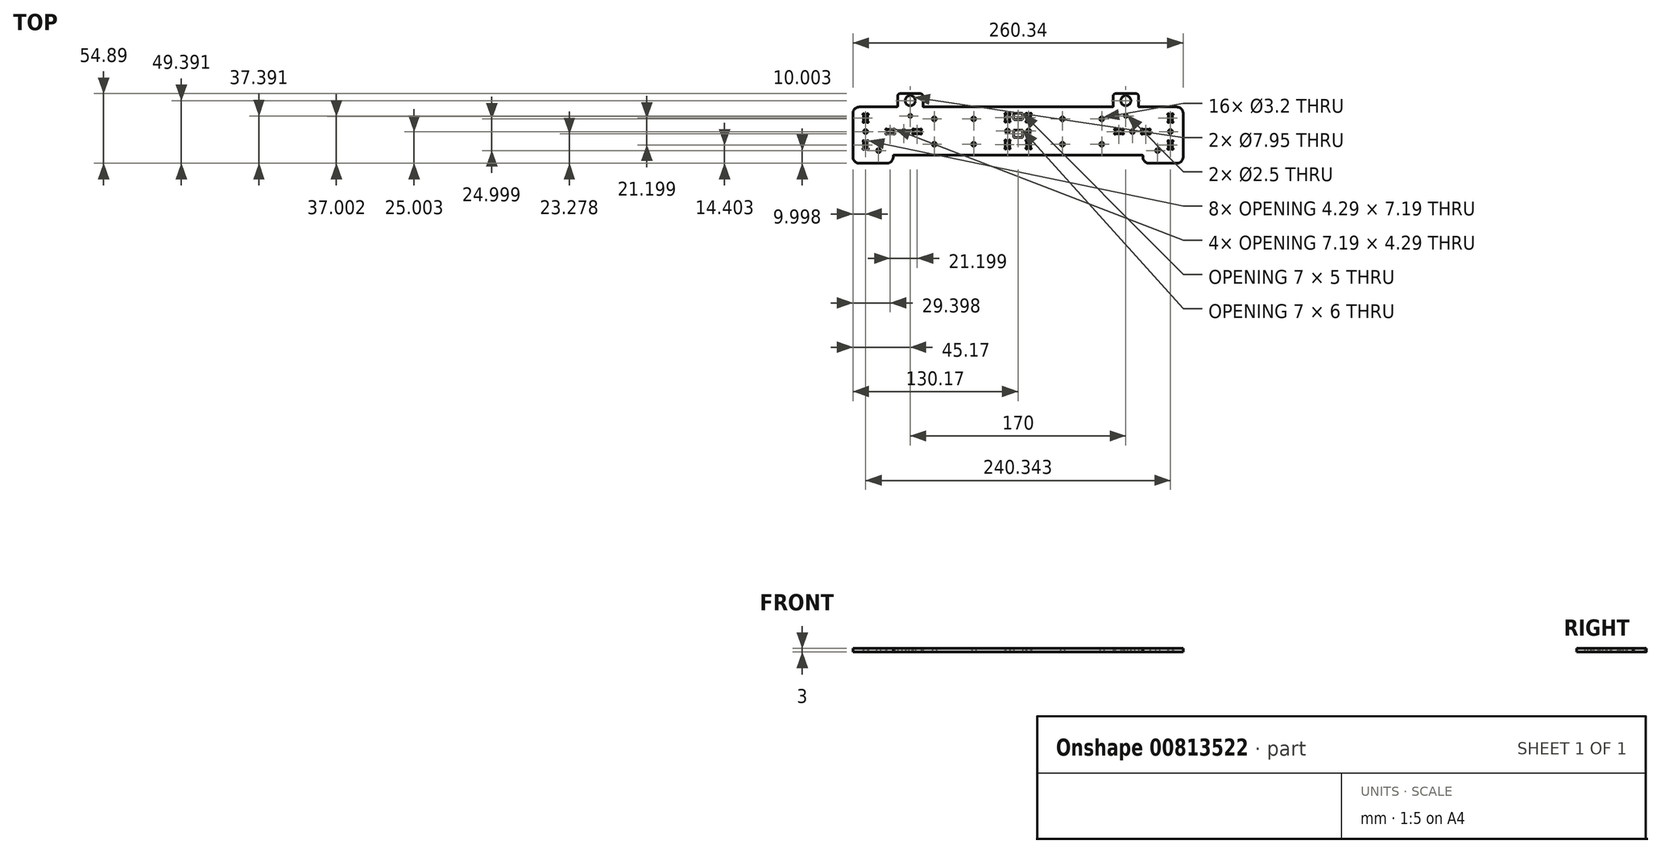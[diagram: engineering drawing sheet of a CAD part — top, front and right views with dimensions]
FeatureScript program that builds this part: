
annotation { "Feature Type Name" : "Feature", "Feature Type Description" : "" }
export const myFeature = defineFeature(function(context is Context, id is Id, definition is map)
    precondition{}
    {
        {
            var Q0;
            Q0=qCreatedBy(makeId("Top.planeOp"),FACE);
            var sketch = newSketch(context, id + "F0", { "sketchPlane" : qUnion([Q0])});
            skArc(sketch, "E0", {"start": v(-130.17, -20.39) * mm, "mid": v(-128.7, -23.92) * mm, "end": v(-125.17, -25.39) * mm});
            skLineSegment(sketch, "E1", {"start": v(-130.17, -20.39) * mm, "end": v(-130.17, 14) * mm});
            skArc(sketch, "E2", {"start": v(-125.17, 19) * mm, "mid": v(-128.7, 17.54) * mm, "end": v(-130.17, 14) * mm});
            skLineSegment(sketch, "E3", {"start": v(-125.17, 19) * mm, "end": v(-95.5, 19) * mm});
            skArc(sketch, "E4", {"start": v(-95.5, 19) * mm, "mid": v(-95.15, 19.15) * mm, "end": v(-95, 19.5) * mm});
            skArc(sketch, "E5", {"start": v(-75, 19.5) * mm, "mid": v(-74.85, 19.15) * mm, "end": v(-74.5, 19) * mm});
            skLineSegment(sketch, "E6", {"start": v(-74.5, 19) * mm, "end": v(74.5, 19) * mm});
            skArc(sketch, "E7", {"start": v(74.5, 19) * mm, "mid": v(74.85, 19.15) * mm, "end": v(75, 19.5) * mm});
            skArc(sketch, "E8", {"start": v(95, 19.5) * mm, "mid": v(95.15, 19.15) * mm, "end": v(95.5, 19) * mm});
            skLineSegment(sketch, "E9", {"start": v(95.5, 19) * mm, "end": v(125.17, 19) * mm});
            skArc(sketch, "E10", {"start": v(130.17, 14) * mm, "mid": v(128.7, 17.54) * mm, "end": v(125.17, 19) * mm});
            skLineSegment(sketch, "E11", {"start": v(130.17, 14) * mm, "end": v(130.17, -20.39) * mm});
            skArc(sketch, "E12", {"start": v(125.17, -25.39) * mm, "mid": v(128.7, -23.92) * mm, "end": v(130.17, -20.39) * mm});
            skArc(sketch, "E13", {"start": v(118.95, -7.64) * mm, "mid": v(119.14, -7.82) * mm, "end": v(119.39, -7.89) * mm});
            skArc(sketch, "E14", {"start": v(118.95, -7.64) * mm, "mid": v(118.17, -7.53) * mm, "end": v(118.27, -8.32) * mm});
            skArc(sketch, "E15", {"start": v(118.52, -8.75) * mm, "mid": v(118.45, -8.5) * mm, "end": v(118.27, -8.32) * mm});
            skLineSegment(sketch, "E16", {"start": v(118.52, -8.75) * mm, "end": v(118.52, -13.22) * mm});
            skArc(sketch, "E17", {"start": v(118.27, -13.65) * mm, "mid": v(118.45, -13.47) * mm, "end": v(118.52, -13.22) * mm});
            skArc(sketch, "E18", {"start": v(118.27, -13.65) * mm, "mid": v(118.17, -14.44) * mm, "end": v(118.95, -14.34) * mm});
            skArc(sketch, "E19", {"start": v(119.39, -14.09) * mm, "mid": v(119.14, -14.15) * mm, "end": v(118.95, -14.34) * mm});
            skLineSegment(sketch, "E20", {"start": v(119.39, -14.09) * mm, "end": v(120.96, -14.09) * mm});
            skArc(sketch, "E21", {"start": v(121.39, -14.34) * mm, "mid": v(121.2, -14.15) * mm, "end": v(120.96, -14.09) * mm});
            skArc(sketch, "E22", {"start": v(121.39, -14.34) * mm, "mid": v(122.17, -14.44) * mm, "end": v(122.07, -13.65) * mm});
            skArc(sketch, "E23", {"start": v(121.82, -13.22) * mm, "mid": v(121.89, -13.47) * mm, "end": v(122.07, -13.65) * mm});
            skLineSegment(sketch, "E24", {"start": v(121.82, -13.22) * mm, "end": v(121.82, -8.75) * mm});
            skArc(sketch, "E25", {"start": v(122.07, -8.32) * mm, "mid": v(121.89, -8.5) * mm, "end": v(121.82, -8.75) * mm});
            skArc(sketch, "E26", {"start": v(122.07, -8.32) * mm, "mid": v(122.17, -7.53) * mm, "end": v(121.39, -7.64) * mm});
            skArc(sketch, "E27", {"start": v(120.96, -7.89) * mm, "mid": v(121.2, -7.82) * mm, "end": v(121.39, -7.64) * mm});
            skLineSegment(sketch, "E28", {"start": v(120.96, -7.89) * mm, "end": v(119.39, -7.89) * mm});
            skArc(sketch, "E29", {"start": v(118.95, 13.56) * mm, "mid": v(119.14, 13.38) * mm, "end": v(119.39, 13.31) * mm});
            skArc(sketch, "E30", {"start": v(118.95, 13.56) * mm, "mid": v(118.17, 13.67) * mm, "end": v(118.27, 12.88) * mm});
            skArc(sketch, "E31", {"start": v(118.52, 12.45) * mm, "mid": v(118.45, 12.7) * mm, "end": v(118.27, 12.88) * mm});
            skLineSegment(sketch, "E32", {"start": v(118.52, 12.45) * mm, "end": v(118.52, 7.98) * mm});
            skArc(sketch, "E33", {"start": v(118.27, 7.55) * mm, "mid": v(118.45, 7.73) * mm, "end": v(118.52, 7.98) * mm});
            skArc(sketch, "E34", {"start": v(118.27, 7.55) * mm, "mid": v(118.17, 6.76) * mm, "end": v(118.95, 6.86) * mm});
            skArc(sketch, "E35", {"start": v(119.39, 7.11) * mm, "mid": v(119.14, 7.05) * mm, "end": v(118.95, 6.86) * mm});
            skLineSegment(sketch, "E36", {"start": v(119.39, 7.11) * mm, "end": v(120.96, 7.11) * mm});
            skArc(sketch, "E37", {"start": v(121.39, 6.86) * mm, "mid": v(121.2, 7.05) * mm, "end": v(120.96, 7.11) * mm});
            skArc(sketch, "E38", {"start": v(121.39, 6.86) * mm, "mid": v(122.17, 6.76) * mm, "end": v(122.07, 7.55) * mm});
            skArc(sketch, "E39", {"start": v(121.82, 7.98) * mm, "mid": v(121.89, 7.73) * mm, "end": v(122.07, 7.55) * mm});
            skLineSegment(sketch, "E40", {"start": v(121.82, 7.98) * mm, "end": v(121.82, 12.45) * mm});
            skArc(sketch, "E41", {"start": v(122.07, 12.88) * mm, "mid": v(121.89, 12.7) * mm, "end": v(121.82, 12.45) * mm});
            skArc(sketch, "E42", {"start": v(122.07, 12.88) * mm, "mid": v(122.17, 13.67) * mm, "end": v(121.39, 13.56) * mm});
            skArc(sketch, "E43", {"start": v(120.96, 13.31) * mm, "mid": v(121.2, 13.38) * mm, "end": v(121.39, 13.56) * mm});
            skLineSegment(sketch, "E44", {"start": v(120.96, 13.31) * mm, "end": v(119.39, 13.31) * mm});
            skArc(sketch, "E45", {"start": v(-119.39, -7.89) * mm, "mid": v(-119.14, -7.82) * mm, "end": v(-118.95, -7.64) * mm});
            skArc(sketch, "E46", {"start": v(-118.27, -8.32) * mm, "mid": v(-118.17, -7.53) * mm, "end": v(-118.95, -7.64) * mm});
            skArc(sketch, "E47", {"start": v(-118.27, -8.32) * mm, "mid": v(-118.45, -8.5) * mm, "end": v(-118.52, -8.75) * mm});
            skLineSegment(sketch, "E48", {"start": v(-118.52, -8.75) * mm, "end": v(-118.52, -13.22) * mm});
            skArc(sketch, "E49", {"start": v(-118.52, -13.22) * mm, "mid": v(-118.45, -13.47) * mm, "end": v(-118.27, -13.65) * mm});
            skArc(sketch, "E50", {"start": v(-118.95, -14.34) * mm, "mid": v(-118.17, -14.44) * mm, "end": v(-118.27, -13.65) * mm});
            skArc(sketch, "E51", {"start": v(-118.95, -14.34) * mm, "mid": v(-119.14, -14.15) * mm, "end": v(-119.39, -14.09) * mm});
            skLineSegment(sketch, "E52", {"start": v(-119.39, -14.09) * mm, "end": v(-120.96, -14.09) * mm});
            skArc(sketch, "E53", {"start": v(-120.96, -14.09) * mm, "mid": v(-121.2, -14.15) * mm, "end": v(-121.39, -14.34) * mm});
            skArc(sketch, "E54", {"start": v(-122.07, -13.65) * mm, "mid": v(-122.17, -14.44) * mm, "end": v(-121.39, -14.34) * mm});
            skArc(sketch, "E55", {"start": v(-122.07, -13.65) * mm, "mid": v(-121.89, -13.47) * mm, "end": v(-121.82, -13.22) * mm});
            skLineSegment(sketch, "E56", {"start": v(-121.82, -13.22) * mm, "end": v(-121.82, -8.75) * mm});
            skArc(sketch, "E57", {"start": v(-121.82, -8.75) * mm, "mid": v(-121.89, -8.5) * mm, "end": v(-122.07, -8.32) * mm});
            skArc(sketch, "E58", {"start": v(-121.39, -7.64) * mm, "mid": v(-122.17, -7.53) * mm, "end": v(-122.07, -8.32) * mm});
            skArc(sketch, "E59", {"start": v(-121.39, -7.64) * mm, "mid": v(-121.2, -7.82) * mm, "end": v(-120.96, -7.89) * mm});
            skLineSegment(sketch, "E60", {"start": v(-120.96, -7.89) * mm, "end": v(-119.39, -7.89) * mm});
            skArc(sketch, "E61", {"start": v(-119.39, 13.31) * mm, "mid": v(-119.14, 13.38) * mm, "end": v(-118.95, 13.56) * mm});
            skArc(sketch, "E62", {"start": v(-118.27, 12.88) * mm, "mid": v(-118.17, 13.67) * mm, "end": v(-118.95, 13.56) * mm});
            skArc(sketch, "E63", {"start": v(-118.27, 12.88) * mm, "mid": v(-118.45, 12.7) * mm, "end": v(-118.52, 12.45) * mm});
            skLineSegment(sketch, "E64", {"start": v(-118.52, 12.45) * mm, "end": v(-118.52, 7.98) * mm});
            skArc(sketch, "E65", {"start": v(-118.52, 7.98) * mm, "mid": v(-118.45, 7.73) * mm, "end": v(-118.27, 7.55) * mm});
            skArc(sketch, "E66", {"start": v(-118.95, 6.86) * mm, "mid": v(-118.17, 6.76) * mm, "end": v(-118.27, 7.55) * mm});
            skArc(sketch, "E67", {"start": v(-118.95, 6.86) * mm, "mid": v(-119.14, 7.05) * mm, "end": v(-119.39, 7.11) * mm});
            skLineSegment(sketch, "E68", {"start": v(-119.39, 7.11) * mm, "end": v(-120.96, 7.11) * mm});
            skArc(sketch, "E69", {"start": v(-120.96, 7.11) * mm, "mid": v(-121.2, 7.05) * mm, "end": v(-121.39, 6.86) * mm});
            skArc(sketch, "E70", {"start": v(-122.07, 7.55) * mm, "mid": v(-122.17, 6.76) * mm, "end": v(-121.39, 6.86) * mm});
            skArc(sketch, "E71", {"start": v(-122.07, 7.55) * mm, "mid": v(-121.89, 7.73) * mm, "end": v(-121.82, 7.98) * mm});
            skLineSegment(sketch, "E72", {"start": v(-121.82, 7.98) * mm, "end": v(-121.82, 12.45) * mm});
            skArc(sketch, "E73", {"start": v(-121.82, 12.45) * mm, "mid": v(-121.89, 12.7) * mm, "end": v(-122.07, 12.88) * mm});
            skArc(sketch, "E74", {"start": v(-121.39, 13.56) * mm, "mid": v(-122.17, 13.67) * mm, "end": v(-122.07, 12.88) * mm});
            skArc(sketch, "E75", {"start": v(-121.39, 13.56) * mm, "mid": v(-121.2, 13.38) * mm, "end": v(-120.96, 13.31) * mm});
            skLineSegment(sketch, "E76", {"start": v(-120.96, 13.31) * mm, "end": v(-119.39, 13.31) * mm});
            skCircle(sketch, "E77", {"center": v(120.17, -0.39) * mm, "radius": 1.6 * mm});
            skCircle(sketch, "E78", {"center": v(66, -10.39) * mm, "radius": 1.6 * mm});
            skCircle(sketch, "E79", {"center": v(66, 9.61) * mm, "radius": 1.6 * mm});
            skCircle(sketch, "E80", {"center": v(35, -10.39) * mm, "radius": 1.6 * mm});
            skCircle(sketch, "E81", {"center": v(35, 9.61) * mm, "radius": 1.6 * mm});
            skCircle(sketch, "E82", {"center": v(-35, -10.39) * mm, "radius": 1.6 * mm});
            skCircle(sketch, "E83", {"center": v(-35, 9.61) * mm, "radius": 1.6 * mm});
            skCircle(sketch, "E84", {"center": v(-66, -10.39) * mm, "radius": 1.6 * mm});
            skCircle(sketch, "E85", {"center": v(-66, 9.61) * mm, "radius": 1.6 * mm});
            skCircle(sketch, "E86", {"center": v(-120.17, -0.39) * mm, "radius": 1.6 * mm});
            skCircle(sketch, "E87", {"center": v(-85, 12) * mm, "radius": 1.25 * mm});
            skCircle(sketch, "E88", {"center": v(85, 12) * mm, "radius": 1.25 * mm});
            skArc(sketch, "E89", {"start": v(-97.42, 0.83) * mm, "mid": v(-97.6, 0.65) * mm, "end": v(-97.67, 0.4) * mm});
            skArc(sketch, "E90", {"start": v(-97.42, 0.83) * mm, "mid": v(-97.32, 1.62) * mm, "end": v(-98.1, 1.51) * mm});
            skArc(sketch, "E91", {"start": v(-98.54, 1.26) * mm, "mid": v(-98.29, 1.33) * mm, "end": v(-98.1, 1.51) * mm});
            skLineSegment(sketch, "E92", {"start": v(-98.54, 1.26) * mm, "end": v(-103, 1.26) * mm});
            skArc(sketch, "E93", {"start": v(-103.44, 1.51) * mm, "mid": v(-103.26, 1.33) * mm, "end": v(-103, 1.26) * mm});
            skArc(sketch, "E94", {"start": v(-103.44, 1.51) * mm, "mid": v(-104.23, 1.62) * mm, "end": v(-104.12, 0.83) * mm});
            skArc(sketch, "E95", {"start": v(-103.87, 0.4) * mm, "mid": v(-103.94, 0.65) * mm, "end": v(-104.12, 0.83) * mm});
            skLineSegment(sketch, "E96", {"start": v(-103.87, 0.4) * mm, "end": v(-103.87, -1.17) * mm});
            skArc(sketch, "E97", {"start": v(-104.12, -1.6) * mm, "mid": v(-103.94, -1.42) * mm, "end": v(-103.87, -1.17) * mm});
            skArc(sketch, "E98", {"start": v(-104.12, -1.6) * mm, "mid": v(-104.23, -2.4) * mm, "end": v(-103.44, -2.29) * mm});
            skArc(sketch, "E99", {"start": v(-103, -2.04) * mm, "mid": v(-103.26, -2.1) * mm, "end": v(-103.44, -2.29) * mm});
            skLineSegment(sketch, "E100", {"start": v(-103, -2.04) * mm, "end": v(-98.54, -2.04) * mm});
            skArc(sketch, "E101", {"start": v(-98.1, -2.29) * mm, "mid": v(-98.29, -2.1) * mm, "end": v(-98.54, -2.04) * mm});
            skArc(sketch, "E102", {"start": v(-98.1, -2.29) * mm, "mid": v(-97.32, -2.4) * mm, "end": v(-97.42, -1.6) * mm});
            skArc(sketch, "E103", {"start": v(-97.67, -1.17) * mm, "mid": v(-97.6, -1.42) * mm, "end": v(-97.42, -1.6) * mm});
            skLineSegment(sketch, "E104", {"start": v(-97.67, -1.17) * mm, "end": v(-97.67, 0.4) * mm});
            skArc(sketch, "E105", {"start": v(-76.22, 0.83) * mm, "mid": v(-76.4, 0.65) * mm, "end": v(-76.47, 0.4) * mm});
            skArc(sketch, "E106", {"start": v(-76.22, 0.83) * mm, "mid": v(-76.12, 1.62) * mm, "end": v(-76.9, 1.51) * mm});
            skArc(sketch, "E107", {"start": v(-77.34, 1.26) * mm, "mid": v(-77.09, 1.33) * mm, "end": v(-76.9, 1.51) * mm});
            skLineSegment(sketch, "E108", {"start": v(-77.34, 1.26) * mm, "end": v(-81.8, 1.26) * mm});
            skArc(sketch, "E109", {"start": v(-82.24, 1.51) * mm, "mid": v(-82.06, 1.33) * mm, "end": v(-81.8, 1.26) * mm});
            skArc(sketch, "E110", {"start": v(-82.24, 1.51) * mm, "mid": v(-83.03, 1.62) * mm, "end": v(-82.92, 0.83) * mm});
            skArc(sketch, "E111", {"start": v(-82.67, 0.4) * mm, "mid": v(-82.74, 0.65) * mm, "end": v(-82.92, 0.83) * mm});
            skLineSegment(sketch, "E112", {"start": v(-82.67, 0.4) * mm, "end": v(-82.67, -1.17) * mm});
            skArc(sketch, "E113", {"start": v(-82.92, -1.6) * mm, "mid": v(-82.74, -1.42) * mm, "end": v(-82.67, -1.17) * mm});
            skArc(sketch, "E114", {"start": v(-82.92, -1.6) * mm, "mid": v(-83.03, -2.4) * mm, "end": v(-82.24, -2.29) * mm});
            skArc(sketch, "E115", {"start": v(-81.8, -2.04) * mm, "mid": v(-82.06, -2.1) * mm, "end": v(-82.24, -2.29) * mm});
            skLineSegment(sketch, "E116", {"start": v(-81.8, -2.04) * mm, "end": v(-77.34, -2.04) * mm});
            skArc(sketch, "E117", {"start": v(-76.9, -2.29) * mm, "mid": v(-77.09, -2.1) * mm, "end": v(-77.34, -2.04) * mm});
            skArc(sketch, "E118", {"start": v(-76.9, -2.29) * mm, "mid": v(-76.12, -2.4) * mm, "end": v(-76.22, -1.6) * mm});
            skArc(sketch, "E119", {"start": v(-76.47, -1.17) * mm, "mid": v(-76.4, -1.42) * mm, "end": v(-76.22, -1.6) * mm});
            skLineSegment(sketch, "E120", {"start": v(-76.47, -1.17) * mm, "end": v(-76.47, 0.4) * mm});
            skCircle(sketch, "E121", {"center": v(-90.17, -0.39) * mm, "radius": 1.6 * mm});
            skArc(sketch, "E122", {"start": v(82.92, 0.83) * mm, "mid": v(82.74, 0.65) * mm, "end": v(82.67, 0.4) * mm});
            skArc(sketch, "E123", {"start": v(82.92, 0.83) * mm, "mid": v(83.03, 1.62) * mm, "end": v(82.24, 1.51) * mm});
            skArc(sketch, "E124", {"start": v(81.8, 1.26) * mm, "mid": v(82.06, 1.33) * mm, "end": v(82.24, 1.51) * mm});
            skLineSegment(sketch, "E125", {"start": v(81.8, 1.26) * mm, "end": v(77.34, 1.26) * mm});
            skArc(sketch, "E126", {"start": v(76.9, 1.51) * mm, "mid": v(77.09, 1.33) * mm, "end": v(77.34, 1.26) * mm});
            skArc(sketch, "E127", {"start": v(76.9, 1.51) * mm, "mid": v(76.12, 1.62) * mm, "end": v(76.22, 0.83) * mm});
            skArc(sketch, "E128", {"start": v(76.47, 0.4) * mm, "mid": v(76.4, 0.65) * mm, "end": v(76.22, 0.83) * mm});
            skLineSegment(sketch, "E129", {"start": v(76.47, 0.4) * mm, "end": v(76.47, -1.17) * mm});
            skArc(sketch, "E130", {"start": v(76.22, -1.6) * mm, "mid": v(76.4, -1.42) * mm, "end": v(76.47, -1.17) * mm});
            skArc(sketch, "E131", {"start": v(76.22, -1.6) * mm, "mid": v(76.12, -2.4) * mm, "end": v(76.9, -2.29) * mm});
            skArc(sketch, "E132", {"start": v(77.34, -2.04) * mm, "mid": v(77.09, -2.1) * mm, "end": v(76.9, -2.29) * mm});
            skLineSegment(sketch, "E133", {"start": v(77.34, -2.04) * mm, "end": v(81.8, -2.04) * mm});
            skArc(sketch, "E134", {"start": v(82.24, -2.29) * mm, "mid": v(82.06, -2.1) * mm, "end": v(81.8, -2.04) * mm});
            skArc(sketch, "E135", {"start": v(82.24, -2.29) * mm, "mid": v(83.03, -2.4) * mm, "end": v(82.92, -1.6) * mm});
            skArc(sketch, "E136", {"start": v(82.67, -1.17) * mm, "mid": v(82.74, -1.42) * mm, "end": v(82.92, -1.6) * mm});
            skLineSegment(sketch, "E137", {"start": v(82.67, -1.17) * mm, "end": v(82.67, 0.4) * mm});
            skArc(sketch, "E138", {"start": v(104.12, 0.83) * mm, "mid": v(103.94, 0.65) * mm, "end": v(103.87, 0.4) * mm});
            skArc(sketch, "E139", {"start": v(104.12, 0.83) * mm, "mid": v(104.23, 1.62) * mm, "end": v(103.44, 1.51) * mm});
            skArc(sketch, "E140", {"start": v(103, 1.26) * mm, "mid": v(103.26, 1.33) * mm, "end": v(103.44, 1.51) * mm});
            skLineSegment(sketch, "E141", {"start": v(103, 1.26) * mm, "end": v(98.54, 1.26) * mm});
            skArc(sketch, "E142", {"start": v(98.1, 1.51) * mm, "mid": v(98.29, 1.33) * mm, "end": v(98.54, 1.26) * mm});
            skArc(sketch, "E143", {"start": v(98.1, 1.51) * mm, "mid": v(97.32, 1.62) * mm, "end": v(97.42, 0.83) * mm});
            skArc(sketch, "E144", {"start": v(97.67, 0.4) * mm, "mid": v(97.6, 0.65) * mm, "end": v(97.42, 0.83) * mm});
            skLineSegment(sketch, "E145", {"start": v(97.67, 0.4) * mm, "end": v(97.67, -1.17) * mm});
            skArc(sketch, "E146", {"start": v(97.42, -1.6) * mm, "mid": v(97.6, -1.42) * mm, "end": v(97.67, -1.17) * mm});
            skArc(sketch, "E147", {"start": v(97.42, -1.6) * mm, "mid": v(97.32, -2.4) * mm, "end": v(98.1, -2.29) * mm});
            skArc(sketch, "E148", {"start": v(98.54, -2.04) * mm, "mid": v(98.29, -2.1) * mm, "end": v(98.1, -2.29) * mm});
            skLineSegment(sketch, "E149", {"start": v(98.54, -2.04) * mm, "end": v(103, -2.04) * mm});
            skArc(sketch, "E150", {"start": v(103.44, -2.29) * mm, "mid": v(103.26, -2.1) * mm, "end": v(103, -2.04) * mm});
            skArc(sketch, "E151", {"start": v(103.44, -2.29) * mm, "mid": v(104.23, -2.4) * mm, "end": v(104.12, -1.6) * mm});
            skArc(sketch, "E152", {"start": v(103.87, -1.17) * mm, "mid": v(103.94, -1.42) * mm, "end": v(104.12, -1.6) * mm});
            skLineSegment(sketch, "E153", {"start": v(103.87, -1.17) * mm, "end": v(103.87, 0.4) * mm});
            skCircle(sketch, "E154", {"center": v(90.17, -0.39) * mm, "radius": 1.6 * mm});
            skLineSegment(sketch, "E155", {"start": v(-103.44, -25.39) * mm, "end": v(-125.17, -25.39) * mm});
            skArc(sketch, "E156", {"start": v(-103.44, -25.39) * mm, "mid": v(-99.9, -23.92) * mm, "end": v(-98.44, -20.39) * mm});
            skLineSegment(sketch, "E157", {"start": v(125.17, -25.39) * mm, "end": v(103.44, -25.39) * mm});
            skArc(sketch, "E158", {"start": v(98.44, -20.39) * mm, "mid": v(99.9, -23.92) * mm, "end": v(103.44, -25.39) * mm});
            skLineSegment(sketch, "E159", {"start": v(-98.44, -20.39) * mm, "end": v(-98.44, -19.5) * mm});
            skArc(sketch, "E160", {"start": v(-97.94, -19) * mm, "mid": v(-98.3, -19.15) * mm, "end": v(-98.44, -19.5) * mm});
            skLineSegment(sketch, "E161", {"start": v(98.44, -20.39) * mm, "end": v(98.44, -19.5) * mm});
            skLineSegment(sketch, "E162", {"start": v(-97.94, -19) * mm, "end": v(97.94, -19) * mm});
            skArc(sketch, "E163", {"start": v(98.44, -19.5) * mm, "mid": v(98.3, -19.15) * mm, "end": v(97.94, -19) * mm});
            skCircle(sketch, "E164", {"center": v(-8.3, 0) * mm, "radius": 1.6 * mm});
            skArc(sketch, "E165", {"start": v(-9.52, -7.25) * mm, "mid": v(-9.33, -7.43) * mm, "end": v(-9.08, -7.5) * mm});
            skArc(sketch, "E166", {"start": v(-9.52, -7.25) * mm, "mid": v(-10.3, -7.15) * mm, "end": v(-10.2, -7.93) * mm});
            skArc(sketch, "E167", {"start": v(-9.95, -8.37) * mm, "mid": v(-10.02, -8.12) * mm, "end": v(-10.2, -7.93) * mm});
            skLineSegment(sketch, "E168", {"start": v(-9.95, -8.37) * mm, "end": v(-9.95, -12.83) * mm});
            skArc(sketch, "E169", {"start": v(-10.2, -13.27) * mm, "mid": v(-10.02, -13.08) * mm, "end": v(-9.95, -12.83) * mm});
            skArc(sketch, "E170", {"start": v(-10.2, -13.27) * mm, "mid": v(-10.3, -14.05) * mm, "end": v(-9.52, -13.95) * mm});
            skArc(sketch, "E171", {"start": v(-9.08, -13.7) * mm, "mid": v(-9.33, -13.77) * mm, "end": v(-9.52, -13.95) * mm});
            skLineSegment(sketch, "E172", {"start": v(-9.08, -13.7) * mm, "end": v(-7.52, -13.7) * mm});
            skArc(sketch, "E173", {"start": v(-7.08, -13.95) * mm, "mid": v(-7.27, -13.77) * mm, "end": v(-7.52, -13.7) * mm});
            skArc(sketch, "E174", {"start": v(-7.08, -13.95) * mm, "mid": v(-6.3, -14.05) * mm, "end": v(-6.4, -13.27) * mm});
            skArc(sketch, "E175", {"start": v(-6.65, -12.83) * mm, "mid": v(-6.58, -13.08) * mm, "end": v(-6.4, -13.27) * mm});
            skLineSegment(sketch, "E176", {"start": v(-6.65, -12.83) * mm, "end": v(-6.65, -8.37) * mm});
            skArc(sketch, "E177", {"start": v(-6.4, -7.93) * mm, "mid": v(-6.58, -8.12) * mm, "end": v(-6.65, -8.37) * mm});
            skArc(sketch, "E178", {"start": v(-6.4, -7.93) * mm, "mid": v(-6.3, -7.15) * mm, "end": v(-7.08, -7.25) * mm});
            skArc(sketch, "E179", {"start": v(-7.52, -7.5) * mm, "mid": v(-7.27, -7.43) * mm, "end": v(-7.08, -7.25) * mm});
            skLineSegment(sketch, "E180", {"start": v(-7.52, -7.5) * mm, "end": v(-9.08, -7.5) * mm});
            skArc(sketch, "E181", {"start": v(-9.52, 13.95) * mm, "mid": v(-9.33, 13.77) * mm, "end": v(-9.08, 13.7) * mm});
            skArc(sketch, "E182", {"start": v(-9.52, 13.95) * mm, "mid": v(-10.3, 14.05) * mm, "end": v(-10.2, 13.27) * mm});
            skArc(sketch, "E183", {"start": v(-9.95, 12.83) * mm, "mid": v(-10.02, 13.08) * mm, "end": v(-10.2, 13.27) * mm});
            skLineSegment(sketch, "E184", {"start": v(-9.95, 12.83) * mm, "end": v(-9.95, 8.37) * mm});
            skArc(sketch, "E185", {"start": v(-10.2, 7.93) * mm, "mid": v(-10.02, 8.12) * mm, "end": v(-9.95, 8.37) * mm});
            skArc(sketch, "E186", {"start": v(-10.2, 7.93) * mm, "mid": v(-10.3, 7.15) * mm, "end": v(-9.52, 7.25) * mm});
            skArc(sketch, "E187", {"start": v(-9.08, 7.5) * mm, "mid": v(-9.33, 7.43) * mm, "end": v(-9.52, 7.25) * mm});
            skLineSegment(sketch, "E188", {"start": v(-9.08, 7.5) * mm, "end": v(-7.52, 7.5) * mm});
            skArc(sketch, "E189", {"start": v(-7.08, 7.25) * mm, "mid": v(-7.27, 7.43) * mm, "end": v(-7.52, 7.5) * mm});
            skArc(sketch, "E190", {"start": v(-7.08, 7.25) * mm, "mid": v(-6.3, 7.15) * mm, "end": v(-6.4, 7.93) * mm});
            skArc(sketch, "E191", {"start": v(-6.65, 8.37) * mm, "mid": v(-6.58, 8.12) * mm, "end": v(-6.4, 7.93) * mm});
            skLineSegment(sketch, "E192", {"start": v(-6.65, 8.37) * mm, "end": v(-6.65, 12.83) * mm});
            skArc(sketch, "E193", {"start": v(-6.4, 13.27) * mm, "mid": v(-6.58, 13.08) * mm, "end": v(-6.65, 12.83) * mm});
            skArc(sketch, "E194", {"start": v(-6.4, 13.27) * mm, "mid": v(-6.3, 14.05) * mm, "end": v(-7.08, 13.95) * mm});
            skArc(sketch, "E195", {"start": v(-7.52, 13.7) * mm, "mid": v(-7.27, 13.77) * mm, "end": v(-7.08, 13.95) * mm});
            skLineSegment(sketch, "E196", {"start": v(-7.52, 13.7) * mm, "end": v(-9.08, 13.7) * mm});
            skCircle(sketch, "E197", {"center": v(8.3, 0) * mm, "radius": 1.6 * mm});
            skArc(sketch, "E198", {"start": v(7.08, -7.25) * mm, "mid": v(7.27, -7.43) * mm, "end": v(7.52, -7.5) * mm});
            skArc(sketch, "E199", {"start": v(7.08, -7.25) * mm, "mid": v(6.3, -7.15) * mm, "end": v(6.4, -7.93) * mm});
            skArc(sketch, "E200", {"start": v(6.65, -8.37) * mm, "mid": v(6.58, -8.12) * mm, "end": v(6.4, -7.93) * mm});
            skLineSegment(sketch, "E201", {"start": v(6.65, -8.37) * mm, "end": v(6.65, -12.83) * mm});
            skArc(sketch, "E202", {"start": v(6.4, -13.27) * mm, "mid": v(6.58, -13.08) * mm, "end": v(6.65, -12.83) * mm});
            skArc(sketch, "E203", {"start": v(6.4, -13.27) * mm, "mid": v(6.3, -14.05) * mm, "end": v(7.08, -13.95) * mm});
            skArc(sketch, "E204", {"start": v(7.52, -13.7) * mm, "mid": v(7.27, -13.77) * mm, "end": v(7.08, -13.95) * mm});
            skLineSegment(sketch, "E205", {"start": v(7.52, -13.7) * mm, "end": v(9.08, -13.7) * mm});
            skArc(sketch, "E206", {"start": v(9.52, -13.95) * mm, "mid": v(9.33, -13.77) * mm, "end": v(9.08, -13.7) * mm});
            skArc(sketch, "E207", {"start": v(9.52, -13.95) * mm, "mid": v(10.3, -14.05) * mm, "end": v(10.2, -13.27) * mm});
            skArc(sketch, "E208", {"start": v(9.95, -12.83) * mm, "mid": v(10.02, -13.08) * mm, "end": v(10.2, -13.27) * mm});
            skLineSegment(sketch, "E209", {"start": v(9.95, -12.83) * mm, "end": v(9.95, -8.37) * mm});
            skArc(sketch, "E210", {"start": v(10.2, -7.93) * mm, "mid": v(10.02, -8.12) * mm, "end": v(9.95, -8.37) * mm});
            skArc(sketch, "E211", {"start": v(10.2, -7.93) * mm, "mid": v(10.3, -7.15) * mm, "end": v(9.52, -7.25) * mm});
            skArc(sketch, "E212", {"start": v(9.08, -7.5) * mm, "mid": v(9.33, -7.43) * mm, "end": v(9.52, -7.25) * mm});
            skLineSegment(sketch, "E213", {"start": v(9.08, -7.5) * mm, "end": v(7.52, -7.5) * mm});
            skArc(sketch, "E214", {"start": v(7.08, 13.95) * mm, "mid": v(7.27, 13.77) * mm, "end": v(7.52, 13.7) * mm});
            skArc(sketch, "E215", {"start": v(7.08, 13.95) * mm, "mid": v(6.3, 14.05) * mm, "end": v(6.4, 13.27) * mm});
            skArc(sketch, "E216", {"start": v(6.65, 12.83) * mm, "mid": v(6.58, 13.08) * mm, "end": v(6.4, 13.27) * mm});
            skLineSegment(sketch, "E217", {"start": v(6.65, 12.83) * mm, "end": v(6.65, 8.37) * mm});
            skArc(sketch, "E218", {"start": v(6.4, 7.93) * mm, "mid": v(6.58, 8.12) * mm, "end": v(6.65, 8.37) * mm});
            skArc(sketch, "E219", {"start": v(6.4, 7.93) * mm, "mid": v(6.3, 7.15) * mm, "end": v(7.08, 7.25) * mm});
            skArc(sketch, "E220", {"start": v(7.52, 7.5) * mm, "mid": v(7.27, 7.43) * mm, "end": v(7.08, 7.25) * mm});
            skLineSegment(sketch, "E221", {"start": v(7.52, 7.5) * mm, "end": v(9.08, 7.5) * mm});
            skArc(sketch, "E222", {"start": v(9.52, 7.25) * mm, "mid": v(9.33, 7.43) * mm, "end": v(9.08, 7.5) * mm});
            skArc(sketch, "E223", {"start": v(9.52, 7.25) * mm, "mid": v(10.3, 7.15) * mm, "end": v(10.2, 7.93) * mm});
            skArc(sketch, "E224", {"start": v(9.95, 8.37) * mm, "mid": v(10.02, 8.12) * mm, "end": v(10.2, 7.93) * mm});
            skLineSegment(sketch, "E225", {"start": v(9.95, 8.37) * mm, "end": v(9.95, 12.83) * mm});
            skArc(sketch, "E226", {"start": v(10.2, 13.27) * mm, "mid": v(10.02, 13.08) * mm, "end": v(9.95, 12.83) * mm});
            skArc(sketch, "E227", {"start": v(10.2, 13.27) * mm, "mid": v(10.3, 14.05) * mm, "end": v(9.52, 13.95) * mm});
            skArc(sketch, "E228", {"start": v(9.08, 13.7) * mm, "mid": v(9.33, 13.77) * mm, "end": v(9.52, 13.95) * mm});
            skLineSegment(sketch, "E229", {"start": v(9.08, 13.7) * mm, "end": v(7.52, 13.7) * mm});
            skCircle(sketch, "E230", {"center": v(-85, 24) * mm, "radius": 3.97 * mm});
            skCircle(sketch, "E231", {"center": v(85, 24) * mm, "radius": 3.97 * mm});
            skLineSegment(sketch, "E232", {"start": v(-95, 19.5) * mm, "end": v(-95, 27.5) * mm});
            skLineSegment(sketch, "E233", {"start": v(-75, 27.5) * mm, "end": v(-75, 19.5) * mm});
            skArc(sketch, "E234", {"start": v(-93, 29.5) * mm, "mid": v(-94.41, 28.92) * mm, "end": v(-95, 27.5) * mm});
            skLineSegment(sketch, "E235", {"start": v(-93, 29.5) * mm, "end": v(-77, 29.5) * mm});
            skArc(sketch, "E236", {"start": v(-75, 27.5) * mm, "mid": v(-75.59, 28.92) * mm, "end": v(-77, 29.5) * mm});
            skLineSegment(sketch, "E237", {"start": v(75, 19.5) * mm, "end": v(75, 27.5) * mm});
            skLineSegment(sketch, "E238", {"start": v(95, 27.5) * mm, "end": v(95, 19.5) * mm});
            skArc(sketch, "E239", {"start": v(77, 29.5) * mm, "mid": v(75.59, 28.92) * mm, "end": v(75, 27.5) * mm});
            skLineSegment(sketch, "E240", {"start": v(77, 29.5) * mm, "end": v(93, 29.5) * mm});
            skArc(sketch, "E241", {"start": v(95, 27.5) * mm, "mid": v(94.41, 28.92) * mm, "end": v(93, 29.5) * mm});
            skArc(sketch, "E242", {"start": v(-3.5, 9.51) * mm, "mid": v(-3.38, 9.23) * mm, "end": v(-3.1, 9.11) * mm});
            skLineSegment(sketch, "E243", {"start": v(3.1, 9.11) * mm, "end": v(-3.1, 9.11) * mm});
            skArc(sketch, "E244", {"start": v(3.1, 9.11) * mm, "mid": v(3.38, 9.23) * mm, "end": v(3.5, 9.51) * mm});
            skArc(sketch, "E245", {"start": v(3.5, 0.49) * mm, "mid": v(3.38, 0.77) * mm, "end": v(3.1, 0.89) * mm});
            skLineSegment(sketch, "E246", {"start": v(-3.1, 0.89) * mm, "end": v(3.1, 0.89) * mm});
            skArc(sketch, "E247", {"start": v(-3.1, 0.89) * mm, "mid": v(-3.38, 0.77) * mm, "end": v(-3.5, 0.49) * mm});
            skArc(sketch, "E248", {"start": v(3.1, -5.11) * mm, "mid": v(3.38, -5) * mm, "end": v(3.5, -4.71) * mm});
            skLineSegment(sketch, "E249", {"start": v(3.1, -5.11) * mm, "end": v(-3.1, -5.11) * mm});
            skArc(sketch, "E250", {"start": v(-3.5, -4.71) * mm, "mid": v(-3.38, -5) * mm, "end": v(-3.1, -5.11) * mm});
            skLineSegment(sketch, "E251", {"start": v(3.5, 0.49) * mm, "end": v(3.5, -4.71) * mm});
            skLineSegment(sketch, "E252", {"start": v(-3.5, -4.71) * mm, "end": v(-3.5, 0.49) * mm});
            skArc(sketch, "E253", {"start": v(-3.1, 14.11) * mm, "mid": v(-3.38, 14) * mm, "end": v(-3.5, 13.71) * mm});
            skLineSegment(sketch, "E254", {"start": v(-3.1, 14.11) * mm, "end": v(3.1, 14.11) * mm});
            skArc(sketch, "E255", {"start": v(3.5, 13.71) * mm, "mid": v(3.38, 14) * mm, "end": v(3.1, 14.11) * mm});
            skLineSegment(sketch, "E256", {"start": v(-3.5, 9.51) * mm, "end": v(-3.5, 13.71) * mm});
            skLineSegment(sketch, "E257", {"start": v(3.5, 13.71) * mm, "end": v(3.5, 9.51) * mm});
            skCircle(sketch, "E258", {"center": v(-110, -15.39) * mm, "radius": 1.6 * mm});
            skCircle(sketch, "E259", {"center": v(110, -15.39) * mm, "radius": 1.6 * mm});
            skSolve(sketch);
        }
        {
            var Q0;
            Q0=makeQuery(id+"F0.imprint","IMPRINT",FACE,{"disambiguationData":[TD([[makeQuery(id+"F0.imprint","IMPRINT",EDGE,{"derivedFrom":sQuery(id+"F0.wireOp",EDGE,"E0")}),1.0]])]});
            extrude(context, id + "F1", {"entities" : qUnion([Q0]), "endBound" : BoundingType.SYMMETRIC, "depth" : 3 * mm, "offsetDistance" : 25 * mm});
        }
    });
